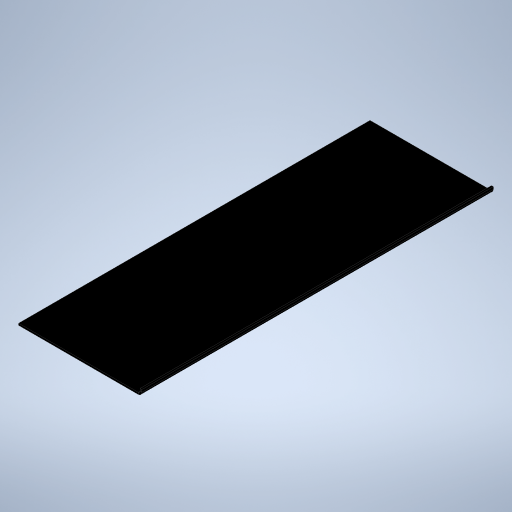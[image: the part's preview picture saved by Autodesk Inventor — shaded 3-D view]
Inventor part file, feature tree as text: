
AUTODESK INVENTOR PART (.ipt)
format: ipt  version: 2023 (Build 270158000, 158)  size: 247,808 bytes
history: native  units: in
note: dims shown in document units (in); Inventor stores cm internally (conversion verified against a paired STEP export)
features: sheet_metal_op x4, sketch x2, other x2
ambient origin geometry x8: Origin, YZ Plane, XZ Plane, XY Plane, X Axis, Y Axis, Z Axis, Center Point
bodies: Solid1 (feature_tree)
feature tree (8):
  sheet_metal_op  "Face1"
  sheet_metal_op  "Flange1"
  sketch  "Sketch1"  dims[d0=7.6378in]
  other  "Plate1"
  sketch  "Sketch3"  dims[d1=22.4409in d2=3.8189in d3=11.2205in d4=0.12in d5=0.12in d6=0.06in d7=0.24in d8=0.12in d9=0.3937in d10=90.0deg d11=0.12in d12=0.48in d13=0.12in d14=0.12in]
  other  "Plate2"
  sheet_metal_op  "Bend1"
  sheet_metal_op  "Corner1"
